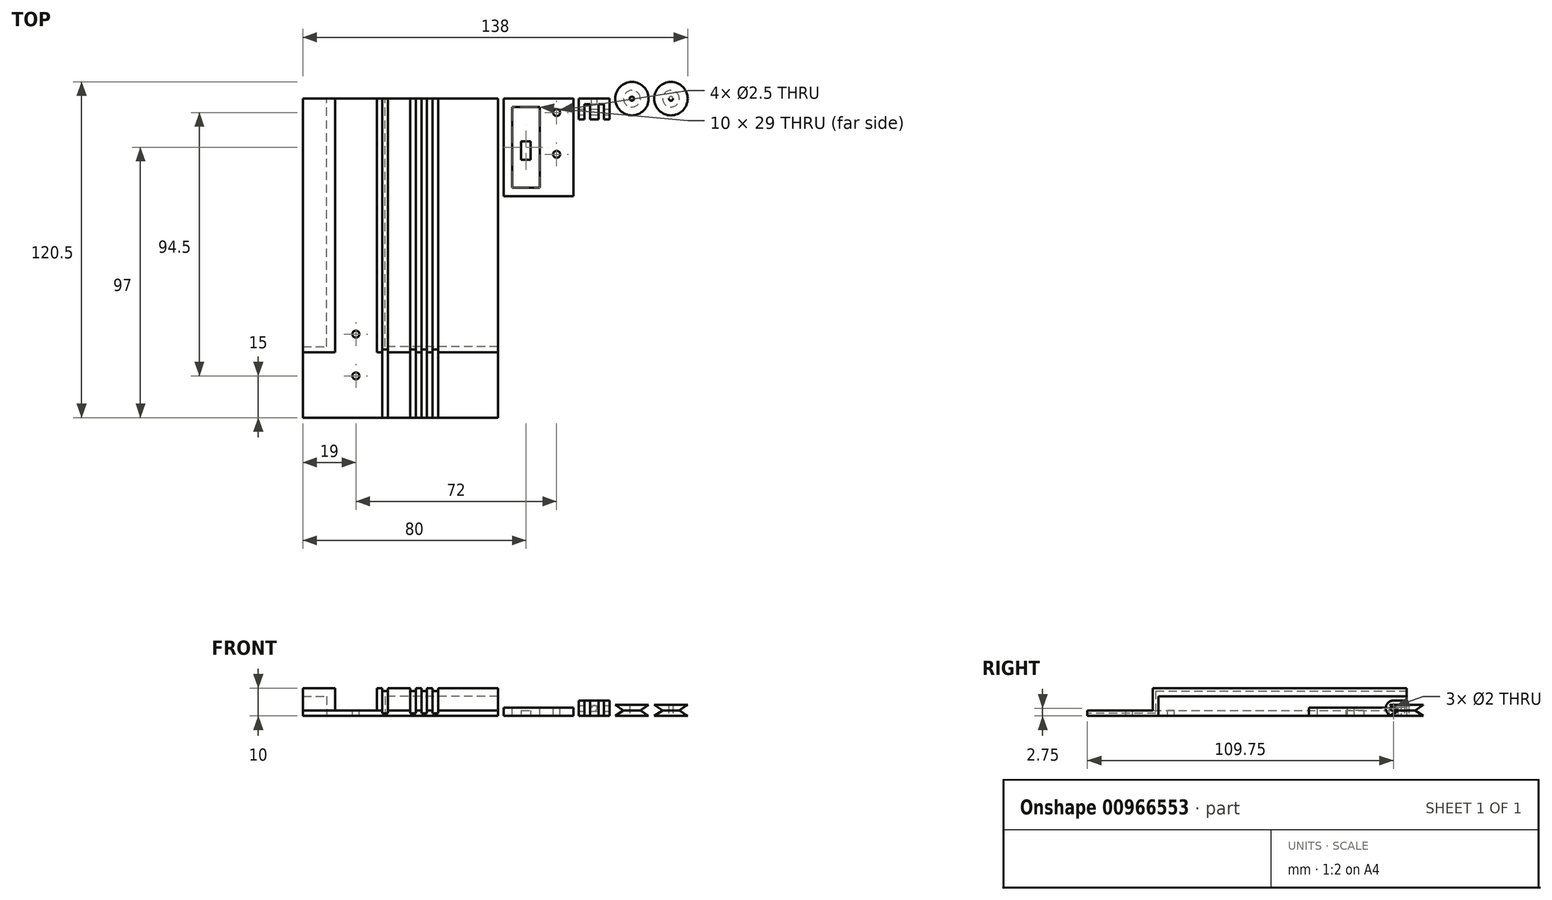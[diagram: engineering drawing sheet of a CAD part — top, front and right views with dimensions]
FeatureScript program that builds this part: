
annotation { "Feature Type Name" : "Feature", "Feature Type Description" : "" }
export const myFeature = defineFeature(function(context is Context, id is Id, definition is map)
    precondition{}
    {
        {
            var Q0;
            Q0=qCreatedBy(makeId("Front.planeOp"),FACE);
            var sketch = newSketch(context, id + "F0", { "sketchPlane" : qUnion([Q0])});
            skLineSegment(sketch, "E0", {"start": v(-70, 10) * mm, "end": v(-70, 7) * mm});
            skLineSegment(sketch, "E1", {"start": v(-70, 7) * mm, "end": v(-61.5, 7) * mm});
            skLineSegment(sketch, "E2", {"start": v(-61.5, 7) * mm, "end": v(-61.5, 0) * mm});
            skLineSegment(sketch, "E3", {"start": v(-61.5, 0) * mm, "end": v(-40.5, 0) * mm});
            skLineSegment(sketch, "E4", {"start": v(-40.5, 0) * mm, "end": v(-40.5, 7) * mm});
            skLineSegment(sketch, "E5", {"start": v(-40.5, 7) * mm, "end": v(0, 7) * mm});
            skLineSegment(sketch, "E6", {"start": v(0, 7) * mm, "end": v(0, 10) * mm});
            skLineSegment(sketch, "E7", {"start": v(0, 10) * mm, "end": v(-43.5, 10) * mm});
            skLineSegment(sketch, "E8", {"start": v(-43.5, 10) * mm, "end": v(-43.5, 2) * mm});
            skLineSegment(sketch, "E9", {"start": v(-43.5, 2) * mm, "end": v(-58.5, 2) * mm});
            skLineSegment(sketch, "E10", {"start": v(-58.5, 2) * mm, "end": v(-58.5, 10) * mm});
            skLineSegment(sketch, "E11", {"start": v(-58.5, 10) * mm, "end": v(-70, 10) * mm});
            skSolve(sketch);
        }
        {
            var Q0;
            Q0=makeQuery(id+"F0.imprint","IMPRINT",FACE,{"disambiguationData":[TD([[makeQuery(id+"F0.imprint","IMPRINT",EDGE,{"derivedFrom":sQuery(id+"F0.wireOp",EDGE,"E0")}),1.0]])]});
            extrude(context, id + "F1", {"entities" : qUnion([Q0]), "depth" : 91 * mm, "offsetDistance" : 25 * mm});
        }
        {
            var Q0;
            Q0=makeQuery(id+"F1.opExtrude","SWEPT_FACE",FACE,{"disambiguationData":[OSD([sQuery(id+"F0.wireOp",EDGE,"E4")])]});
            var sketch = newSketch(context, id + "F2", { "sketchPlane" : qUnion([Q0])});
            skLineSegment(sketch, "E12.bottom", {"start": v(-91, 7) * mm, "end": v(-89, 7) * mm});
            skLineSegment(sketch, "E12.top", {"start": v(-91, 0) * mm, "end": v(-89, 0) * mm});
            skLineSegment(sketch, "E12.left", {"start": v(-91, 7) * mm, "end": v(-91, 0) * mm});
            skLineSegment(sketch, "E12.right", {"start": v(-89, 7) * mm, "end": v(-89, 0) * mm});
            skSolve(sketch);
        }
        {
            var Q0;
            Q0=makeQuery(id+"F2.imprint","IMPRINT",FACE,{"disambiguationData":[TD([[makeQuery(id+"F2.imprint","IMPRINT",EDGE,{"derivedFrom":sQuery(id+"F2.wireOp",EDGE,"E12.bottom")}),-1.0]])]});
            extrude(context, id + "F3", {"entities" : qUnion([Q0]), "operationType" : NewBodyOperationType.ADD, "depth" : 40.5 * mm, "offsetDistance" : 25 * mm});
        }
        {
            var Q0;
            Q0=makeQuery(id+"F1.opExtrude","SWEPT_FACE",FACE,{"disambiguationData":[OSD([sQuery(id+"F0.wireOp",EDGE,"E2")])]});
            var sketch = newSketch(context, id + "F4", { "sketchPlane" : qUnion([Q0])});
            skLineSegment(sketch, "E13.bottom", {"start": v(91, 7) * mm, "end": v(89, 7) * mm});
            skLineSegment(sketch, "E13.top", {"start": v(91, 0) * mm, "end": v(89, 0) * mm});
            skLineSegment(sketch, "E13.left", {"start": v(91, 7) * mm, "end": v(91, 0) * mm});
            skLineSegment(sketch, "E13.right", {"start": v(89, 7) * mm, "end": v(89, 0) * mm});
            skSolve(sketch);
        }
        {
            var Q0;
            Q0=makeQuery(id+"F4.imprint","IMPRINT",FACE,{"disambiguationData":[TD([[makeQuery(id+"F4.imprint","IMPRINT",EDGE,{"derivedFrom":sQuery(id+"F4.wireOp",EDGE,"E13.bottom")}),1.0]])]});
            extrude(context, id + "F5", {"entities" : qUnion([Q0]), "operationType" : NewBodyOperationType.ADD, "depth" : 8.5 * mm, "offsetDistance" : 25 * mm});
        }
        {
            var Q0;
            Q0=makeQuery(id+"F5.boolean.opBoolean","MERGE",FACE,{"derivedFrom":[makeQuery(id+"F3.boolean.opBoolean","MERGE",FACE,{"derivedFrom":[makeQuery(id+"F1.opExtrude","CAP_FACE",FACE,{"disambiguationData":[OSD([sQuery(id+"F0.wireOp",EDGE,"E0"),sQuery(id+"F0.wireOp",EDGE,"E1"),sQuery(id+"F0.wireOp",EDGE,"E2"),sQuery(id+"F0.wireOp",EDGE,"E3"),sQuery(id+"F0.wireOp",EDGE,"E4"),sQuery(id+"F0.wireOp",EDGE,"E5"),sQuery(id+"F0.wireOp",EDGE,"E6"),sQuery(id+"F0.wireOp",EDGE,"E7"),sQuery(id+"F0.wireOp",EDGE,"E8"),sQuery(id+"F0.wireOp",EDGE,"E9"),sQuery(id+"F0.wireOp",EDGE,"E10"),sQuery(id+"F0.wireOp",EDGE,"E11")])],"isStart":false}),makeQuery(id+"F3.opExtrude","SWEPT_FACE",FACE,{"disambiguationData":[OSD([sQuery(id+"F2.wireOp",EDGE,"E12.left")])]})]}),makeQuery(id+"F5.opExtrude","SWEPT_FACE",FACE,{"disambiguationData":[OSD([sQuery(id+"F4.wireOp",EDGE,"E13.left")])]})]});
            var sketch = newSketch(context, id + "F6", { "sketchPlane" : qUnion([Q0])});
            skLineSegment(sketch, "E14.bottom", {"start": v(-70, 2) * mm, "end": v(0, 2) * mm});
            skLineSegment(sketch, "E14.top", {"start": v(-70, 0) * mm, "end": v(0, 0) * mm});
            skLineSegment(sketch, "E14.left", {"start": v(-70, 2) * mm, "end": v(-70, 0) * mm});
            skLineSegment(sketch, "E14.right", {"start": v(0, 2) * mm, "end": v(0, 0) * mm});
            skSolve(sketch);
        }
        {
            var Q0;
            Q0=makeQuery(id+"F6.imprint","IMPRINT",FACE,{"disambiguationData":[TD([[makeQuery(id+"F6.imprint","IMPRINT",EDGE,{"derivedFrom":sQuery(id+"F6.wireOp",EDGE,"E14.top")}),1.0]])]});
            extrude(context, id + "F7", {"entities" : qUnion([Q0]), "operationType" : NewBodyOperationType.ADD, "depth" : 23.5 * mm, "offsetDistance" : 25 * mm});
        }
        {
            var Q0;
            Q0=makeQuery(id+"F1.opExtrude","SWEPT_FACE",FACE,{"disambiguationData":[OSD([sQuery(id+"F0.wireOp",EDGE,"E7")])]});
            var sketch = newSketch(context, id + "F8", { "sketchPlane" : qUnion([Q0])});
            skLineSegment(sketch, "E15.bottom", {"start": v(-41.5, -91) * mm, "end": v(-39.5, -91) * mm});
            skLineSegment(sketch, "E15.top", {"start": v(-41.5, 0) * mm, "end": v(-39.5, 0) * mm});
            skLineSegment(sketch, "E15.left", {"start": v(-41.5, -91) * mm, "end": v(-41.5, 0) * mm});
            skLineSegment(sketch, "E15.right", {"start": v(-39.5, -91) * mm, "end": v(-39.5, 0) * mm});
            skLineSegment(sketch, "E16.bottom", {"start": v(-31.5, -91) * mm, "end": v(-29.5, -91) * mm});
            skLineSegment(sketch, "E16.top", {"start": v(-31.5, 0) * mm, "end": v(-29.5, 0) * mm});
            skLineSegment(sketch, "E16.left", {"start": v(-31.5, -91) * mm, "end": v(-31.5, 0) * mm});
            skLineSegment(sketch, "E16.right", {"start": v(-29.5, -91) * mm, "end": v(-29.5, 0) * mm});
            skLineSegment(sketch, "E17.bottom", {"start": v(-27.5, -91) * mm, "end": v(-25.5, -91) * mm});
            skLineSegment(sketch, "E17.top", {"start": v(-27.5, 0) * mm, "end": v(-25.5, 0) * mm});
            skLineSegment(sketch, "E17.left", {"start": v(-27.5, -91) * mm, "end": v(-27.5, 0) * mm});
            skLineSegment(sketch, "E17.right", {"start": v(-25.5, -91) * mm, "end": v(-25.5, 0) * mm});
            skLineSegment(sketch, "E18.bottom", {"start": v(-23.5, -91) * mm, "end": v(-21.5, -91) * mm});
            skLineSegment(sketch, "E18.top", {"start": v(-23.5, 0) * mm, "end": v(-21.5, 0) * mm});
            skLineSegment(sketch, "E18.left", {"start": v(-23.5, -91) * mm, "end": v(-23.5, 0) * mm});
            skLineSegment(sketch, "E18.right", {"start": v(-21.5, -91) * mm, "end": v(-21.5, 0) * mm});
            skSolve(sketch);
        }
        {
            var Q0;
            Q0=makeQuery(id+"F8.imprint","IMPRINT",FACE,{"disambiguationData":[TD([[makeQuery(id+"F8.imprint","IMPRINT",EDGE,{"derivedFrom":sQuery(id+"F8.wireOp",EDGE,"E15.bottom")}),-1.0]])]});
            var Q1;
            Q1=makeQuery(id+"F8.imprint","IMPRINT",FACE,{"disambiguationData":[TD([[makeQuery(id+"F8.imprint","IMPRINT",EDGE,{"derivedFrom":sQuery(id+"F8.wireOp",EDGE,"E16.bottom")}),-1.0]])]});
            var Q2;
            Q2=makeQuery(id+"F8.imprint","IMPRINT",FACE,{"disambiguationData":[TD([[makeQuery(id+"F8.imprint","IMPRINT",EDGE,{"derivedFrom":sQuery(id+"F8.wireOp",EDGE,"E17.bottom")}),-1.0]])]});
            var Q3;
            Q3=makeQuery(id+"F8.imprint","IMPRINT",FACE,{"disambiguationData":[TD([[makeQuery(id+"F8.imprint","IMPRINT",EDGE,{"derivedFrom":sQuery(id+"F8.wireOp",EDGE,"E18.bottom")}),-1.0]])]});
            extrude(context, id + "F9", {"entities" : qUnion([Q0, Q1, Q2, Q3]), "operationType" : NewBodyOperationType.REMOVE, "oppositeDirection" : true, "depth" : 1 * mm, "offsetDistance" : 25 * mm});
        }
        {
            var Q0;
            {var subQ0=sQuery(id+"F0.wireOp",EDGE,"E9");var subQ1=sQuery(id+"F0.wireOp",EDGE,"E8");var subQ2=sQuery(id+"F0.wireOp",EDGE,"E7");var subQ3=sQuery(id+"F0.wireOp",EDGE,"E6");var subQ4=sQuery(id+"F2.wireOp",EDGE,"E12.left");Q0=makeQuery(id+"F7.boolean.opBoolean","SPLIT",FACE,{"disambiguationData":[TD([makeQuery(id+"F1.opExtrude","SWEPT_FACE",FACE,{"disambiguationData":[OSD([subQ3])]})])],"derivedFrom":makeQuery(id+"F5.boolean.opBoolean","MERGE",FACE,{"derivedFrom":[makeQuery(id+"F3.boolean.opBoolean","MERGE",FACE,{"derivedFrom":[makeQuery(id+"F1.opExtrude","CAP_FACE",FACE,{"disambiguationData":[OSD([sQuery(id+"F0.wireOp",EDGE,"E0"),sQuery(id+"F0.wireOp",EDGE,"E1"),sQuery(id+"F0.wireOp",EDGE,"E2"),sQuery(id+"F0.wireOp",EDGE,"E3"),sQuery(id+"F0.wireOp",EDGE,"E4"),sQuery(id+"F0.wireOp",EDGE,"E5"),subQ3,subQ2,subQ1,subQ0,sQuery(id+"F0.wireOp",EDGE,"E10"),sQuery(id+"F0.wireOp",EDGE,"E11")])],"isStart":false}),makeQuery(id+"F3.opExtrude","SWEPT_FACE",FACE,{"disambiguationData":[OSD([subQ4])]})]}),makeQuery(id+"F5.opExtrude","SWEPT_FACE",FACE,{"disambiguationData":[OSD([sQuery(id+"F4.wireOp",EDGE,"E13.left")])]})]})});}
            var sketch = newSketch(context, id + "F10", { "sketchPlane" : qUnion([Q0])});
            skLineSegment(sketch, "E19.bottom", {"start": v(-41.5, 9) * mm, "end": v(-39.5, 9) * mm});
            skLineSegment(sketch, "E19.top", {"start": v(-41.5, 2) * mm, "end": v(-39.5, 2) * mm});
            skLineSegment(sketch, "E19.left", {"start": v(-41.5, 9) * mm, "end": v(-41.5, 2) * mm});
            skLineSegment(sketch, "E19.right", {"start": v(-39.5, 9) * mm, "end": v(-39.5, 2) * mm});
            skLineSegment(sketch, "E20.bottom", {"start": v(-31.5, 9) * mm, "end": v(-29.5, 9) * mm});
            skLineSegment(sketch, "E20.top", {"start": v(-31.5, 2) * mm, "end": v(-29.5, 2) * mm});
            skLineSegment(sketch, "E20.left", {"start": v(-31.5, 9) * mm, "end": v(-31.5, 2) * mm});
            skLineSegment(sketch, "E20.right", {"start": v(-29.5, 9) * mm, "end": v(-29.5, 2) * mm});
            skLineSegment(sketch, "E21.bottom", {"start": v(-27.5, 9) * mm, "end": v(-25.5, 9) * mm});
            skLineSegment(sketch, "E21.top", {"start": v(-27.5, 2) * mm, "end": v(-25.5, 2) * mm});
            skLineSegment(sketch, "E21.left", {"start": v(-27.5, 9) * mm, "end": v(-27.5, 2) * mm});
            skLineSegment(sketch, "E21.right", {"start": v(-25.5, 9) * mm, "end": v(-25.5, 2) * mm});
            skLineSegment(sketch, "E22.bottom", {"start": v(-23.5, 9) * mm, "end": v(-21.5, 9) * mm});
            skLineSegment(sketch, "E22.top", {"start": v(-23.5, 2) * mm, "end": v(-21.5, 2) * mm});
            skLineSegment(sketch, "E22.left", {"start": v(-23.5, 9) * mm, "end": v(-23.5, 2) * mm});
            skLineSegment(sketch, "E22.right", {"start": v(-21.5, 9) * mm, "end": v(-21.5, 2) * mm});
            skSolve(sketch);
        }
        {
            var Q0;
            Q0=makeQuery(id+"F10.imprint","IMPRINT",FACE,{"disambiguationData":[TD([[makeQuery(id+"F10.imprint","IMPRINT",EDGE,{"derivedFrom":sQuery(id+"F10.wireOp",EDGE,"E19.top")}),1.0]])]});
            var Q1;
            Q1=makeQuery(id+"F10.imprint","IMPRINT",FACE,{"disambiguationData":[TD([[makeQuery(id+"F10.imprint","IMPRINT",EDGE,{"derivedFrom":sQuery(id+"F10.wireOp",EDGE,"E20.top")}),1.0]])]});
            var Q2;
            Q2=makeQuery(id+"F10.imprint","IMPRINT",FACE,{"disambiguationData":[TD([[makeQuery(id+"F10.imprint","IMPRINT",EDGE,{"derivedFrom":sQuery(id+"F10.wireOp",EDGE,"E21.bottom")}),1.0]])]});
            var Q3;
            Q3=makeQuery(id+"F10.imprint","IMPRINT",FACE,{"disambiguationData":[TD([[makeQuery(id+"F10.imprint","IMPRINT",EDGE,{"derivedFrom":sQuery(id+"F10.wireOp",EDGE,"E22.top")}),1.0]])]});
            extrude(context, id + "F11", {"entities" : qUnion([Q0, Q1, Q2, Q3]), "operationType" : NewBodyOperationType.REMOVE, "oppositeDirection" : true, "depth" : 1 * mm, "offsetDistance" : 25 * mm});
        }
        {
            var Q0;
            Q0=makeQuery(id+"F11.boolean.opBoolean","MERGE",FACE,{"derivedFrom":[makeQuery(id+"F7.boolean.opBoolean","MERGE",FACE,{"derivedFrom":[makeQuery(id+"F1.opExtrude","SWEPT_FACE",FACE,{"disambiguationData":[OSD([sQuery(id+"F0.wireOp",EDGE,"E9")])]}),makeQuery(id+"F7.opExtrude","SWEPT_FACE",FACE,{"disambiguationData":[OSD([sQuery(id+"F6.wireOp",EDGE,"E14.bottom")])]})]})],"fromTools":[makeQuery(id+"F11.opExtrude","SWEPT_FACE",FACE,{"disambiguationData":[OSD([sQuery(id+"F10.wireOp",EDGE,"E19.top")])]}),makeQuery(id+"F11.opExtrude","SWEPT_FACE",FACE,{"disambiguationData":[OSD([sQuery(id+"F10.wireOp",EDGE,"E20.top")])]}),makeQuery(id+"F11.opExtrude","SWEPT_FACE",FACE,{"disambiguationData":[OSD([sQuery(id+"F10.wireOp",EDGE,"E21.top")])]}),makeQuery(id+"F11.opExtrude","SWEPT_FACE",FACE,{"disambiguationData":[OSD([sQuery(id+"F10.wireOp",EDGE,"E22.top")])]})]});
            var sketch = newSketch(context, id + "F12", { "sketchPlane" : qUnion([Q0])});
            skLineSegment(sketch, "E23.bottom", {"start": v(-41.5, -90) * mm, "end": v(-39.5, -90) * mm});
            skLineSegment(sketch, "E23.top", {"start": v(-41.5, -114.5) * mm, "end": v(-39.5, -114.5) * mm});
            skLineSegment(sketch, "E23.left", {"start": v(-41.5, -90) * mm, "end": v(-41.5, -114.5) * mm});
            skLineSegment(sketch, "E23.right", {"start": v(-39.5, -90) * mm, "end": v(-39.5, -114.5) * mm});
            skLineSegment(sketch, "E24.bottom", {"start": v(-31.5, -90) * mm, "end": v(-29.5, -90) * mm});
            skLineSegment(sketch, "E24.top", {"start": v(-31.5, -114.5) * mm, "end": v(-29.5, -114.5) * mm});
            skLineSegment(sketch, "E24.left", {"start": v(-31.5, -90) * mm, "end": v(-31.5, -114.5) * mm});
            skLineSegment(sketch, "E24.right", {"start": v(-29.5, -90) * mm, "end": v(-29.5, -114.5) * mm});
            skLineSegment(sketch, "E25.bottom", {"start": v(-27.5, -90) * mm, "end": v(-25.5, -90) * mm});
            skLineSegment(sketch, "E25.top", {"start": v(-27.5, -114.5) * mm, "end": v(-25.5, -114.5) * mm});
            skLineSegment(sketch, "E25.left", {"start": v(-27.5, -90) * mm, "end": v(-27.5, -114.5) * mm});
            skLineSegment(sketch, "E25.right", {"start": v(-25.5, -90) * mm, "end": v(-25.5, -114.5) * mm});
            skLineSegment(sketch, "E26.bottom", {"start": v(-23.5, -90) * mm, "end": v(-21.5, -90) * mm});
            skLineSegment(sketch, "E26.top", {"start": v(-23.5, -114.5) * mm, "end": v(-21.5, -114.5) * mm});
            skLineSegment(sketch, "E26.left", {"start": v(-23.5, -90) * mm, "end": v(-23.5, -114.5) * mm});
            skLineSegment(sketch, "E26.right", {"start": v(-21.5, -90) * mm, "end": v(-21.5, -114.5) * mm});
            skSolve(sketch);
        }
        {
            var Q0;
            {var subQ18=sQuery(id+"F12.wireOp",EDGE,"E23.bottom");Q0=makeQuery(id+"F12.imprint","IMPRINT",FACE,{"disambiguationData":[TD([[makeQuery(id+"F12.imprint","IMPRINT",EDGE,{"derivedFrom":subQ18}),-1.0]])]});}
            var Q1;
            {var subQ17=sQuery(id+"F12.wireOp",EDGE,"E24.bottom");Q1=makeQuery(id+"F12.imprint","IMPRINT",FACE,{"disambiguationData":[TD([[makeQuery(id+"F12.imprint","IMPRINT",EDGE,{"derivedFrom":subQ17}),-1.0]])]});}
            var Q2;
            {var subQ17=sQuery(id+"F12.wireOp",EDGE,"E25.bottom");Q2=makeQuery(id+"F12.imprint","IMPRINT",FACE,{"disambiguationData":[TD([[makeQuery(id+"F12.imprint","IMPRINT",EDGE,{"derivedFrom":subQ17}),-1.0]])]});}
            var Q3;
            {var subQ20=sQuery(id+"F12.wireOp",EDGE,"E26.bottom");Q3=makeQuery(id+"F12.imprint","IMPRINT",FACE,{"disambiguationData":[TD([[makeQuery(id+"F12.imprint","IMPRINT",EDGE,{"derivedFrom":subQ20}),-1.0]])]});}
            extrude(context, id + "F13", {"entities" : qUnion([Q0, Q1, Q2, Q3]), "operationType" : NewBodyOperationType.REMOVE, "oppositeDirection" : true, "depth" : 1 * mm, "offsetDistance" : 25 * mm});
        }
        {
            var Q0;
            {var subQ2=sQuery(id+"F0.wireOp",EDGE,"E0");var subQ6=sQuery(id+"F0.wireOp",EDGE,"E9");var subQ14=sQuery(id+"F6.wireOp",EDGE,"E14.bottom");Q0=makeQuery(id+"F13.boolean.opBoolean","SPLIT",FACE,{"disambiguationData":[TD([makeQuery(id+"F1.opExtrude","SWEPT_FACE",FACE,{"disambiguationData":[OSD([subQ2])]})])],"derivedFrom":makeQuery(id+"F11.boolean.opBoolean","MERGE",FACE,{"derivedFrom":[makeQuery(id+"F7.boolean.opBoolean","MERGE",FACE,{"derivedFrom":[makeQuery(id+"F1.opExtrude","SWEPT_FACE",FACE,{"disambiguationData":[OSD([subQ6])]}),makeQuery(id+"F7.opExtrude","SWEPT_FACE",FACE,{"disambiguationData":[OSD([subQ14])]})]})],"fromTools":[makeQuery(id+"F11.opExtrude","SWEPT_FACE",FACE,{"disambiguationData":[OSD([sQuery(id+"F10.wireOp",EDGE,"E19.top")])]}),makeQuery(id+"F11.opExtrude","SWEPT_FACE",FACE,{"disambiguationData":[OSD([sQuery(id+"F10.wireOp",EDGE,"E20.top")])]}),makeQuery(id+"F11.opExtrude","SWEPT_FACE",FACE,{"disambiguationData":[OSD([sQuery(id+"F10.wireOp",EDGE,"E21.top")])]}),makeQuery(id+"F11.opExtrude","SWEPT_FACE",FACE,{"disambiguationData":[OSD([sQuery(id+"F10.wireOp",EDGE,"E22.top")])]})]})});}
            var sketch = newSketch(context, id + "F14", { "sketchPlane" : qUnion([Q0])});
            skCircle(sketch, "E27", {"center": v(-51, -99.5) * mm, "radius": 1.25 * mm});
            skCircle(sketch, "E28", {"center": v(-51, -84.5) * mm, "radius": 1.25 * mm});
            skSolve(sketch);
        }
        {
            var Q0;
            Q0=makeQuery(id+"F14.imprint","IMPRINT",FACE,{"disambiguationData":[TD([[makeQuery(id+"F14.imprint","IMPRINT",EDGE,{"derivedFrom":sQuery(id+"F14.wireOp",EDGE,"E27")}),1.0]])]});
            var Q1;
            Q1=makeQuery(id+"F14.imprint","IMPRINT",FACE,{"disambiguationData":[TD([[makeQuery(id+"F14.imprint","IMPRINT",EDGE,{"derivedFrom":sQuery(id+"F14.wireOp",EDGE,"E28")}),1.0]])]});
            extrude(context, id + "F15", {"entities" : qUnion([Q0, Q1]), "operationType" : NewBodyOperationType.REMOVE, "oppositeDirection" : true, "depth" : 2 * mm, "offsetDistance" : 25 * mm});
        }
        {
            var Q0;
            Q0=qCreatedBy(makeId("Top.planeOp"),FACE);
            var sketch = newSketch(context, id + "F16", { "sketchPlane" : qUnion([Q0])});
            skLineSegment(sketch, "E29.bottom", {"start": v(2, 0) * mm, "end": v(27, 0) * mm});
            skLineSegment(sketch, "E29.top", {"start": v(2, -35) * mm, "end": v(27, -35) * mm});
            skLineSegment(sketch, "E29.left", {"start": v(2, 0) * mm, "end": v(2, -35) * mm});
            skLineSegment(sketch, "E29.right", {"start": v(27, 0) * mm, "end": v(27, -35) * mm});
            skSolve(sketch);
        }
        {
            var Q0;
            Q0=makeQuery(id+"F16.imprint","IMPRINT",FACE,{"disambiguationData":[TD([[makeQuery(id+"F16.imprint","IMPRINT",EDGE,{"derivedFrom":sQuery(id+"F16.wireOp",EDGE,"E29.bottom")}),-1.0]])]});
            extrude(context, id + "F17", {"entities" : qUnion([Q0]), "depth" : 3 * mm, "offsetDistance" : 25 * mm});
        }
        {
            var Q0;
            Q0=makeQuery(id+"F17.opExtrude","CAP_FACE",FACE,{"disambiguationData":[OSD([sQuery(id+"F16.wireOp",EDGE,"E29.bottom"),sQuery(id+"F16.wireOp",EDGE,"E29.top"),sQuery(id+"F16.wireOp",EDGE,"E29.left"),sQuery(id+"F16.wireOp",EDGE,"E29.right")])],"isStart":false});
            var sketch = newSketch(context, id + "F18", { "sketchPlane" : qUnion([Q0])});
            skCircle(sketch, "E30", {"center": v(21, -20) * mm, "radius": 1.25 * mm});
            skCircle(sketch, "E31", {"center": v(21, -5) * mm, "radius": 1.25 * mm});
            skSolve(sketch);
        }
        {
            var Q0;
            Q0=makeQuery(id+"F18.imprint","IMPRINT",FACE,{"disambiguationData":[TD([[makeQuery(id+"F18.imprint","IMPRINT",EDGE,{"derivedFrom":sQuery(id+"F18.wireOp",EDGE,"E30")}),-1.0]])]});
            var sketch = newSketch(context, id + "F19", { "sketchPlane" : qUnion([Q0])});
            skLineSegment(sketch, "E32.bottom", {"start": v(5, -3) * mm, "end": v(15, -3) * mm});
            skLineSegment(sketch, "E32.top", {"start": v(5, -32) * mm, "end": v(15, -32) * mm});
            skLineSegment(sketch, "E32.left", {"start": v(5, -3) * mm, "end": v(5, -32) * mm});
            skLineSegment(sketch, "E32.right", {"start": v(15, -3) * mm, "end": v(15, -32) * mm});
            skSolve(sketch);
        }
        {
            var Q0;
            Q0=makeQuery(id+"F19.imprint","IMPRINT",FACE,{"disambiguationData":[TD([[makeQuery(id+"F19.imprint","IMPRINT",EDGE,{"derivedFrom":sQuery(id+"F19.wireOp",EDGE,"E32.bottom")}),-1.0]])]});
            var Q1;
            Q1=makeQuery(id+"F19.imprint","IMPRINT",FACE,{"disambiguationData":[TD([[makeQuery(id+"F19.imprint","IMPRINT",EDGE,{"derivedFrom":makeQuery(id+"F18.imprint","IMPRINT",EDGE,{"derivedFrom":sQuery(id+"F18.wireOp",EDGE,"E30")})}),1.0]])]});
            var Q2;
            Q2=makeQuery(id+"F19.imprint","IMPRINT",FACE,{"disambiguationData":[TD([[makeQuery(id+"F19.imprint","IMPRINT",EDGE,{"derivedFrom":makeQuery(id+"F18.imprint","IMPRINT",EDGE,{"derivedFrom":sQuery(id+"F18.wireOp",EDGE,"E31")})}),1.0]])]});
            extrude(context, id + "F20", {"entities" : qUnion([Q0, Q1, Q2]), "operationType" : NewBodyOperationType.REMOVE, "oppositeDirection" : true, "depth" : 3 * mm, "offsetDistance" : 25 * mm});
        }
        {
            var Q0;
            Q0=qCreatedBy(makeId("Front.planeOp"),FACE);
            var sketch = newSketch(context, id + "F21", { "sketchPlane" : qUnion([Q0])});
            skLineSegment(sketch, "E33.bottom", {"start": v(29, 5.5) * mm, "end": v(40, 5.5) * mm});
            skLineSegment(sketch, "E33.top", {"start": v(29, 0) * mm, "end": v(40, 0) * mm});
            skLineSegment(sketch, "E33.left", {"start": v(29, 5.5) * mm, "end": v(29, 0) * mm});
            skLineSegment(sketch, "E33.right", {"start": v(40, 5.5) * mm, "end": v(40, 0) * mm});
            skSolve(sketch);
        }
        {
            var Q0;
            Q0=makeQuery(id+"F21.imprint","IMPRINT",FACE,{"disambiguationData":[TD([[makeQuery(id+"F21.imprint","IMPRINT",EDGE,{"derivedFrom":sQuery(id+"F21.wireOp",EDGE,"E33.bottom")}),-1.0]])]});
            extrude(context, id + "F22", {"entities" : qUnion([Q0]), "depth" : 7.5 * mm, "offsetDistance" : 25 * mm});
        }
        {
            var Q0;
            Q0=makeQuery(id+"F22.opExtrude","CAP_FACE",FACE,{"disambiguationData":[OSD([sQuery(id+"F21.wireOp",EDGE,"E33.bottom"),sQuery(id+"F21.wireOp",EDGE,"E33.top"),sQuery(id+"F21.wireOp",EDGE,"E33.left"),sQuery(id+"F21.wireOp",EDGE,"E33.right")])],"isStart":false});
            var sketch = newSketch(context, id + "F23", { "sketchPlane" : qUnion([Q0])});
            skLineSegment(sketch, "E34.bottom", {"start": v(31, 5.5) * mm, "end": v(33, 5.5) * mm});
            skLineSegment(sketch, "E34.top", {"start": v(31, 0) * mm, "end": v(33, 0) * mm});
            skLineSegment(sketch, "E34.left", {"start": v(31, 5.5) * mm, "end": v(31, 0) * mm});
            skLineSegment(sketch, "E34.right", {"start": v(33, 5.5) * mm, "end": v(33, 0) * mm});
            skLineSegment(sketch, "E35.bottom", {"start": v(36, 5.5) * mm, "end": v(38, 5.5) * mm});
            skLineSegment(sketch, "E35.top", {"start": v(36, 0) * mm, "end": v(38, 0) * mm});
            skLineSegment(sketch, "E35.left", {"start": v(36, 5.5) * mm, "end": v(36, 0) * mm});
            skLineSegment(sketch, "E35.right", {"start": v(38, 5.5) * mm, "end": v(38, 0) * mm});
            skSolve(sketch);
        }
        {
            var Q0;
            Q0=makeQuery(id+"F23.imprint","IMPRINT",FACE,{"disambiguationData":[TD([[makeQuery(id+"F23.imprint","IMPRINT",EDGE,{"derivedFrom":sQuery(id+"F23.wireOp",EDGE,"E34.bottom")}),-1.0]])]});
            var Q1;
            Q1=makeQuery(id+"F23.imprint","IMPRINT",FACE,{"disambiguationData":[TD([[makeQuery(id+"F23.imprint","IMPRINT",EDGE,{"derivedFrom":sQuery(id+"F23.wireOp",EDGE,"E35.bottom")}),-1.0]])]});
            extrude(context, id + "F24", {"entities" : qUnion([Q0, Q1]), "operationType" : NewBodyOperationType.REMOVE, "oppositeDirection" : true, "depth" : 5.5 * mm, "offsetDistance" : 25 * mm});
        }
        {
            var Q0;
            {var subQ0=sQuery(id+"F21.wireOp",EDGE,"E33.bottom");var subQ1=sQuery(id+"F21.wireOp",EDGE,"E33.left");Q0=makeQuery(id+"F24.boolean.opBoolean","SPLIT",EDGE,{"disambiguationData":[TD([makeQuery(id+"F22.opExtrude","SWEPT_FACE",FACE,{"disambiguationData":[OSD([subQ1])]})])],"derivedFrom":makeQuery(id+"F22.opExtrude","CAP_EDGE",EDGE,{"disambiguationData":[OSD([subQ0])],"isStart":false})});}
            var Q1;
            {var subQ0=sQuery(id+"F21.wireOp",EDGE,"E33.bottom");Q1=makeQuery(id+"F24.boolean.opBoolean","SPLIT",EDGE,{"disambiguationData":[TD([makeQuery(id+"F24.opExtrude","SWEPT_FACE",FACE,{"disambiguationData":[OSD([sQuery(id+"F23.wireOp",EDGE,"E34.right")])]})])],"derivedFrom":makeQuery(id+"F22.opExtrude","CAP_EDGE",EDGE,{"disambiguationData":[OSD([subQ0])],"isStart":false})});}
            var Q2;
            {var subQ0=sQuery(id+"F21.wireOp",EDGE,"E33.bottom");var subQ1=sQuery(id+"F21.wireOp",EDGE,"E33.right");Q2=makeQuery(id+"F24.boolean.opBoolean","SPLIT",EDGE,{"disambiguationData":[TD([makeQuery(id+"F22.opExtrude","SWEPT_FACE",FACE,{"disambiguationData":[OSD([subQ1])]})])],"derivedFrom":makeQuery(id+"F22.opExtrude","CAP_EDGE",EDGE,{"disambiguationData":[OSD([subQ0])],"isStart":false})});}
            var Q3;
            {var subQ0=sQuery(id+"F21.wireOp",EDGE,"E33.right");var subQ1=sQuery(id+"F21.wireOp",EDGE,"E33.top");Q3=makeQuery(id+"F24.boolean.opBoolean","SPLIT",EDGE,{"disambiguationData":[TD([makeQuery(id+"F22.opExtrude","SWEPT_FACE",FACE,{"disambiguationData":[OSD([subQ0])]})])],"derivedFrom":makeQuery(id+"F22.opExtrude","CAP_EDGE",EDGE,{"disambiguationData":[OSD([subQ1])],"isStart":false})});}
            var Q4;
            {var subQ0=sQuery(id+"F21.wireOp",EDGE,"E33.top");Q4=makeQuery(id+"F24.boolean.opBoolean","SPLIT",EDGE,{"disambiguationData":[TD([makeQuery(id+"F24.opExtrude","SWEPT_FACE",FACE,{"disambiguationData":[OSD([sQuery(id+"F23.wireOp",EDGE,"E34.right")])]})])],"derivedFrom":makeQuery(id+"F22.opExtrude","CAP_EDGE",EDGE,{"disambiguationData":[OSD([subQ0])],"isStart":false})});}
            var Q5;
            {var subQ0=sQuery(id+"F21.wireOp",EDGE,"E33.left");var subQ1=sQuery(id+"F21.wireOp",EDGE,"E33.top");Q5=makeQuery(id+"F24.boolean.opBoolean","SPLIT",EDGE,{"disambiguationData":[TD([makeQuery(id+"F22.opExtrude","SWEPT_FACE",FACE,{"disambiguationData":[OSD([subQ0])]})])],"derivedFrom":makeQuery(id+"F22.opExtrude","CAP_EDGE",EDGE,{"disambiguationData":[OSD([subQ1])],"isStart":false})});}
            fillet(context, id + "F25", {"entities" : qUnion([Q0, Q1, Q2, Q3, Q4, Q5]), "radius" : 2.75 * mm, "tangentPropagation" : true, "allowEdgeOverflow" : false});
        }
        {
            var Q0;
            Q0=makeQuery(id+"F22.opExtrude","SWEPT_FACE",FACE,{"disambiguationData":[OSD([sQuery(id+"F21.wireOp",EDGE,"E33.right")])]});
            var sketch = newSketch(context, id + "F26", { "sketchPlane" : qUnion([Q0])});
            skCircle(sketch, "E36", {"center": v(-4.75, 2.75) * mm, "radius": 1 * mm});
            skSolve(sketch);
        }
        {
            var Q0;
            Q0=makeQuery(id+"F26.imprint","IMPRINT",FACE,{"disambiguationData":[TD([[makeQuery(id+"F26.imprint","IMPRINT",EDGE,{"derivedFrom":sQuery(id+"F26.wireOp",EDGE,"E36")}),1.0]])]});
            extrude(context, id + "F27", {"entities" : qUnion([Q0]), "operationType" : NewBodyOperationType.REMOVE, "oppositeDirection" : true, "depth" : 11 * mm, "offsetDistance" : 25 * mm});
        }
        {
            var Q0;
            Q0=makeQuery(id+"F22.opExtrude","CAP_FACE",FACE,{"disambiguationData":[OSD([sQuery(id+"F21.wireOp",EDGE,"E33.bottom"),sQuery(id+"F21.wireOp",EDGE,"E33.top"),sQuery(id+"F21.wireOp",EDGE,"E33.left"),sQuery(id+"F21.wireOp",EDGE,"E33.right")])],"isStart":true});
            var sketch = newSketch(context, id + "F28", { "sketchPlane" : qUnion([Q0])});
            skCircle(sketch, "E37", {"center": v(-34.5, 2.75) * mm, "radius": 1 * mm});
            skSolve(sketch);
        }
        {
            var Q0;
            Q0=makeQuery(id+"F28.imprint","IMPRINT",FACE,{"disambiguationData":[TD([[makeQuery(id+"F28.imprint","IMPRINT",EDGE,{"derivedFrom":sQuery(id+"F28.wireOp",EDGE,"E37")}),1.0]])]});
            extrude(context, id + "F29", {"entities" : qUnion([Q0]), "operationType" : NewBodyOperationType.REMOVE, "oppositeDirection" : true, "depth" : 2 * mm, "offsetDistance" : 25 * mm});
        }
        {
            var Q0;
            Q0=qCreatedBy(makeId("Top.planeOp"),FACE);
            var sketch = newSketch(context, id + "F30", { "sketchPlane" : qUnion([Q0])});
            skLineSegment(sketch, "E38.bottom", {"start": v(8.3, -15.37) * mm, "end": v(11.7, -15.37) * mm});
            skLineSegment(sketch, "E38.top", {"start": v(8.3, -21.87) * mm, "end": v(11.7, -21.87) * mm});
            skLineSegment(sketch, "E38.left", {"start": v(8.3, -15.37) * mm, "end": v(8.3, -21.87) * mm});
            skLineSegment(sketch, "E38.right", {"start": v(11.7, -15.37) * mm, "end": v(11.7, -21.87) * mm});
            skSolve(sketch);
        }
        {
            var Q0;
            Q0 = qSketchRegion(id + "F30", true);
            extrude(context, id + "F31", {"entities" : qUnion([Q0]), "depth" : 2 * mm, "offsetDistance" : 25 * mm});
        }
        {
            var Q0;
            Q0=qCreatedBy(makeId("Front.planeOp"),FACE);
            var sketch = newSketch(context, id + "F32", { "sketchPlane" : qUnion([Q0])});
            skLineSegment(sketch, "E39", {"start": v(48, 4) * mm, "end": v(48, 0) * mm});
            skLineSegment(sketch, "E40", {"start": v(48, 0) * mm, "end": v(54, 0) * mm});
            skLineSegment(sketch, "E41", {"start": v(54, 0) * mm, "end": v(51, 2) * mm});
            skLineSegment(sketch, "E42", {"start": v(51, 2) * mm, "end": v(54, 3.96) * mm});
            skLineSegment(sketch, "E43", {"start": v(54, 3.96) * mm, "end": v(48, 4) * mm});
            skSolve(sketch);
        }
        {
            var Q0;
            Q0=makeQuery(id+"F32.imprint","IMPRINT",FACE,{"disambiguationData":[TD([[makeQuery(id+"F32.imprint","IMPRINT",EDGE,{"derivedFrom":sQuery(id+"F32.wireOp",EDGE,"E39")}),1.0]])]});
            var Q1;
            Q1=sQuery(id+"F32.wireOp",EDGE,"E39");
            revolve(context, id + "F33", {"surfaceOperationType" : NewSurfaceOperationType.NEW, "entities" : qUnion([Q0]), "axis" : qUnion([Q1]), "revolveType" : RevolveType.FULL});
        }
        {
            var Q0;
            Q0=qCreatedBy(makeId("Front.planeOp"),FACE);
            var sketch = newSketch(context, id + "F34", { "sketchPlane" : qUnion([Q0])});
            skLineSegment(sketch, "E44", {"start": v(62, 4) * mm, "end": v(62, 0) * mm});
            skLineSegment(sketch, "E45", {"start": v(62, 0) * mm, "end": v(68, 0) * mm});
            skLineSegment(sketch, "E46", {"start": v(68, 0) * mm, "end": v(65, 2) * mm});
            skLineSegment(sketch, "E47", {"start": v(65, 2) * mm, "end": v(68, 4.05) * mm});
            skLineSegment(sketch, "E48", {"start": v(68, 4.05) * mm, "end": v(62, 4) * mm});
            skSolve(sketch);
        }
        {
            var Q0;
            Q0=makeQuery(id+"F34.imprint","IMPRINT",FACE,{"disambiguationData":[TD([[makeQuery(id+"F34.imprint","IMPRINT",EDGE,{"derivedFrom":sQuery(id+"F34.wireOp",EDGE,"E44")}),1.0]])]});
            var Q1;
            Q1=sQuery(id+"F34.wireOp",EDGE,"E44");
            revolve(context, id + "F35", {"surfaceOperationType" : NewSurfaceOperationType.NEW, "entities" : qUnion([Q0]), "axis" : qUnion([Q1]), "revolveType" : RevolveType.FULL});
        }
        {
            var Q0;
            Q0=makeQuery(id+"F33.opRevolve","SWEPT_FACE",FACE,{"disambiguationData":[OSD([sQuery(id+"F32.wireOp",EDGE,"E40")])]});
            var sketch = newSketch(context, id + "F36", { "sketchPlane" : qUnion([Q0])});
            skCircle(sketch, "E49", {"center": v(48, 0) * mm, "radius": 0.75 * mm});
            skCircle(sketch, "E50", {"center": v(62, 0) * mm, "radius": 0.75 * mm});
            skSolve(sketch);
        }
        {
            var Q0;
            Q0=makeQuery(id+"F36.imprint","IMPRINT",FACE,{"disambiguationData":[TD([[makeQuery(id+"F36.imprint","IMPRINT",EDGE,{"derivedFrom":sQuery(id+"F36.wireOp",EDGE,"E49")}),1.0]])]});
            var Q1;
            Q1=makeQuery(id+"F36.imprint","IMPRINT",FACE,{"disambiguationData":[TD([[makeQuery(id+"F36.imprint","IMPRINT",EDGE,{"derivedFrom":sQuery(id+"F36.wireOp",EDGE,"E50")}),1.0]])]});
            extrude(context, id + "F37", {"entities" : qUnion([Q0, Q1]), "operationType" : NewBodyOperationType.REMOVE, "oppositeDirection" : true, "depth" : 4 * mm, "offsetDistance" : 25 * mm});
        }
    });
